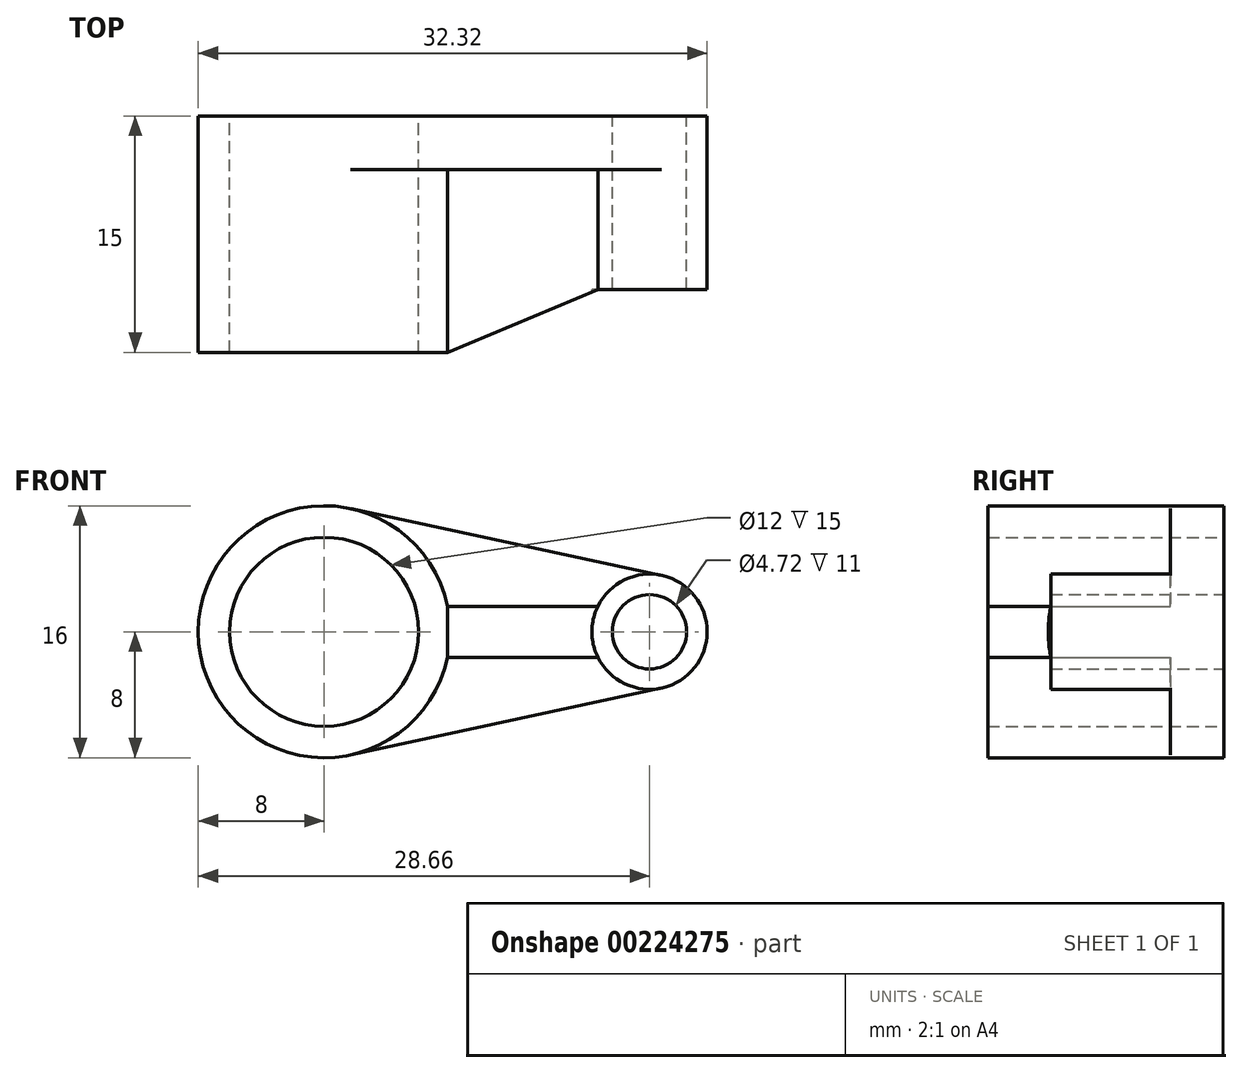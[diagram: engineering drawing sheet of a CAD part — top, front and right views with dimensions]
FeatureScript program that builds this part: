
annotation { "Feature Type Name" : "Feature", "Feature Type Description" : "" }
export const myFeature = defineFeature(function(context is Context, id is Id, definition is map)
    precondition{}
    {
        {
            var Q0;
            Q0=qCreatedBy(makeId("Front.planeOp"),FACE);
            var sketch = newSketch(context, id + "F0", { "sketchPlane" : qUnion([Q0])});
            skCircle(sketch, "E0", {"center": v(0, 0) * mm, "radius": 8 * mm});
            skCircle(sketch, "E1", {"center": v(0, 0) * mm, "radius": 6 * mm});
            skCircle(sketch, "E2", {"center": v(20.66, 0) * mm, "radius": 2.36 * mm});
            skCircle(sketch, "E3", {"center": v(20.66, 0) * mm, "radius": 3.66 * mm});
            skLineSegment(sketch, "E4", {"start": v(1.68, 7.82) * mm, "end": v(21.43, 3.58) * mm});
            skLineSegment(sketch, "E5", {"start": v(1.68, -7.82) * mm, "end": v(21.43, -3.58) * mm});
            skLineSegment(sketch, "E6", {"start": v(7.83, 1.62) * mm, "end": v(17.38, 1.62) * mm});
            skLineSegment(sketch, "E7", {"start": v(7.83, -1.62) * mm, "end": v(17.38, -1.62) * mm});
            skSolve(sketch);
        }
        {
            var Q0;
            Q0=makeQuery(id+"F0.imprint","IMPRINT",FACE,{"disambiguationData":[TD([[makeQuery(id+"F0.imprint","IMPRINT",EDGE,{"derivedFrom":sQuery(id+"F0.wireOp",EDGE,"E1")}),-1.0]])]});
            extrude(context, id + "F1", {"entities" : qUnion([Q0]), "depth" : 15 * mm});
        }
        {
            var Q0;
            {var subQ0=sQuery(id+"F0.wireOp",EDGE,"E6");Q0=makeQuery(id+"F0.imprint","IMPRINT",FACE,{"disambiguationData":[TD([[makeQuery(id+"F0.imprint","IMPRINT",EDGE,{"derivedFrom":subQ0}),-1.0]])]});}
            extrude(context, id + "F2", {"entities" : qUnion([Q0]), "operationType" : NewBodyOperationType.ADD, "depth" : 15 * mm});
        }
        {
            var Q0;
            Q0=makeQuery(id+"F0.imprint","IMPRINT",FACE,{"disambiguationData":[TD([[makeQuery(id+"F0.imprint","IMPRINT",EDGE,{"derivedFrom":sQuery(id+"F0.wireOp",EDGE,"E2")}),-1.0]])]});
            extrude(context, id + "F3", {"entities" : qUnion([Q0]), "operationType" : NewBodyOperationType.ADD, "depth" : 11 * mm});
        }
        {
            var Q0;
            Q0=makeQuery(id+"F2.opExtrude","SWEPT_FACE",FACE,{"disambiguationData":[OSD([sQuery(id+"F0.wireOp",EDGE,"E7")])]});
            var sketch = newSketch(context, id + "F4", { "sketchPlane" : qUnion([Q0])});
            skLineSegment(sketch, "E8", {"start": v(7.83, 15) * mm, "end": v(17.38, 11) * mm});
            skSolve(sketch);
        }
        {
            var Q0;
            Q0=makeQuery(id+"F4.imprint","IMPRINT",FACE,{"disambiguationData":[TD([[makeQuery(id+"F4.imprint","IMPRINT",EDGE,{"derivedFrom":sQuery(id+"F4.wireOp",EDGE,"E8")}),1.0]])]});
            extrude(context, id + "F5", {"entities" : qUnion([Q0]), "operationType" : NewBodyOperationType.REMOVE, "oppositeDirection" : true, "depth" : 25 * mm});
        }
        {
            var Q0;
            {var subQ0=sQuery(id+"F0.wireOp",EDGE,"E4");Q0=makeQuery(id+"F0.imprint","IMPRINT",FACE,{"disambiguationData":[TD([[makeQuery(id+"F0.imprint","IMPRINT",EDGE,{"derivedFrom":subQ0}),-1.0]])]});}
            var Q1;
            {var subQ0=sQuery(id+"F0.wireOp",EDGE,"E5");Q1=makeQuery(id+"F0.imprint","IMPRINT",FACE,{"disambiguationData":[TD([[makeQuery(id+"F0.imprint","IMPRINT",EDGE,{"derivedFrom":subQ0}),1.0]])]});}
            extrude(context, id + "F6", {"entities" : qUnion([Q0, Q1]), "operationType" : NewBodyOperationType.ADD, "depth" : 3.4 * mm});
        }
    });
